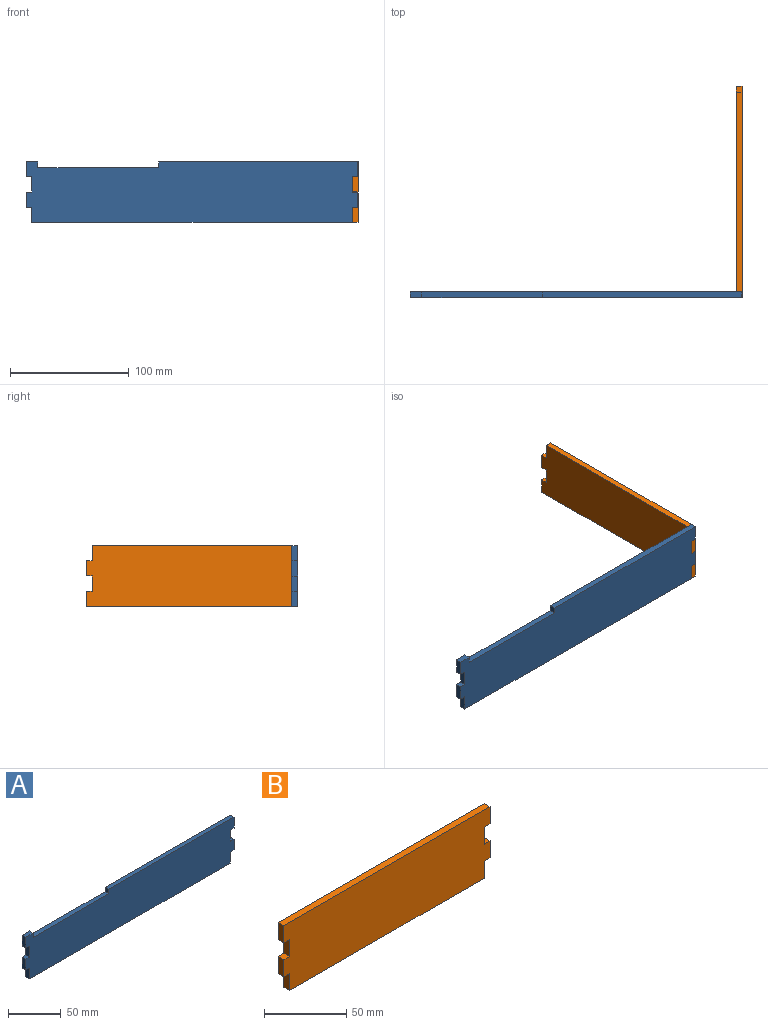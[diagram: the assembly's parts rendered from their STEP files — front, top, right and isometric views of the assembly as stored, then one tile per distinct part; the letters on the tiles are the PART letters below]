
ASSEMBLY  parts=2 mates=1
PART A: 22 faces, bbox 279.4x5x50.8 mm
  f0: plane 167.8x5mm, normal (0,0,1), area 839mm2, adj f1,f19,f20,f21
  f1: plane 5x5mm, normal (-1,0,0), area 25mm2, adj f0,f2,f20,f21
  f2: plane 101.6x5mm, normal (0,0,1), area 508mm2, adj f1,f3,f20,f21
  f3: plane 5x5mm, normal (1,0,0), area 25mm2, adj f2,f4,f20,f21
  f4: plane 10x5mm, normal (0,0,1), area 50mm2, adj f3,f5,f20,f21
  f5: plane 12.7x5mm, normal (-1,0,0), area 63.5mm2, adj f4,f6,f20,f21
  f6: plane 5x5mm, normal (0,0,-1), area 25mm2, adj f5,f7,f20,f21
  f7: plane 12.7x5mm, normal (-1,0,0), area 63.5mm2, adj f6,f8,f20,f21
  f8: plane 5x5mm, normal (0,0,1), area 25mm2, adj f7,f9,f20,f21
  f9: plane 12.7x5mm, normal (-1,0,0), area 63.5mm2, adj f8,f10,f20,f21
  f10: plane 5x5mm, normal (0,0,-1), area 25mm2, adj f9,f11,f20,f21
  f11: plane 12.7x5mm, normal (-1,0,0), area 63.5mm2, adj f10,f12,f20,f21
  f12: plane 269.4x5mm, normal (0,0,-1), area 1347mm2, adj f11,f13,f20,f21
  f13: plane 12.7x5mm, normal (1,0,0), area 63.5mm2, adj f12,f14,f20,f21
  f14: plane 5x5mm, normal (0,0,-1), area 25mm2, adj f13,f15,f20,f21
  f15: plane 12.7x5mm, normal (1,0,0), area 63.5mm2, adj f14,f16,f20,f21
  f16: plane 5x5mm, normal (0,0,1), area 25mm2, adj f15,f17,f20,f21
  f17: plane 12.7x5mm, normal (1,0,0), area 63.5mm2, adj f16,f18,f20,f21
  f18: plane 5x5mm, normal (0,0,-1), area 25mm2, adj f17,f19,f20,f21
  f19: plane 12.7x5mm, normal (1,0,0), area 63.5mm2, adj f0,f18,f20,f21
  f20: plane 279.4x50.8mm, normal (0,-1,0), area 13431.5mm2, adj f0,f1,f2,f3,f4,f5,f6,f7
  f21: plane 279.4x50.8mm, normal (0,1,0), area 13431.5mm2, adj f0,f1,f2,f3,f4,f5,f6,f7
PART B: 18 faces, bbox 177.8x5x50.8 mm
  f0: plane 5x5mm, normal (0,0,-1), area 25mm2, adj f1,f15,f16,f17
  f1: plane 12.7x5mm, normal (1,0,0), area 63.5mm2, adj f0,f2,f16,f17
  f2: plane 177.8x5mm, normal (0,0,1), area 889mm2, adj f1,f3,f16,f17
  f3: plane 12.7x5mm, normal (-1,0,0), area 63.5mm2, adj f2,f4,f16,f17
  f4: plane 5x5mm, normal (0,0,-1), area 25mm2, adj f3,f5,f16,f17
  f5: plane 12.7x5mm, normal (-1,0,0), area 63.5mm2, adj f4,f6,f16,f17
  f6: plane 5x5mm, normal (0,0,1), area 25mm2, adj f5,f7,f16,f17
  f7: plane 12.7x5mm, normal (-1,0,0), area 63.5mm2, adj f6,f8,f16,f17
  f8: plane 5x5mm, normal (0,0,-1), area 25mm2, adj f7,f9,f16,f17
  f9: plane 12.7x5mm, normal (-1,0,0), area 63.5mm2, adj f8,f10,f16,f17
  f10: plane 167.8x5mm, normal (0,0,-1), area 839mm2, adj f9,f11,f16,f17
  f11: plane 12.7x5mm, normal (1,0,0), area 63.5mm2, adj f10,f12,f16,f17
  f12: plane 5x5mm, normal (0,0,-1), area 25mm2, adj f11,f13,f16,f17
  f13: plane 12.7x5mm, normal (1,0,0), area 63.5mm2, adj f12,f14,f16,f17
  f14: plane 5x5mm, normal (0,0,1), area 25mm2, adj f13,f15,f16,f17
  f15: plane 12.7x5mm, normal (1,0,0), area 63.5mm2, adj f0,f14,f16,f17
  f16: plane 177.8x50.8mm, normal (0,-1,0), area 8778.2mm2, adj f0,f1,f2,f3,f4,f5,f6,f7
  f17: plane 177.8x50.8mm, normal (0,1,0), area 8778.2mm2, adj f0,f1,f2,f3,f4,f5,f6,f7
PLACE A t=(-44.33,-2.39,6.71)mm
PLACE B rot(axis=(-0.71,0.71,0),180deg) t=(86.84,81.62,64.88)mm
MATE fastened B.f0 <-> A.f14  axis (0,0,1) through (89.34,-4.89,21.41)mm
